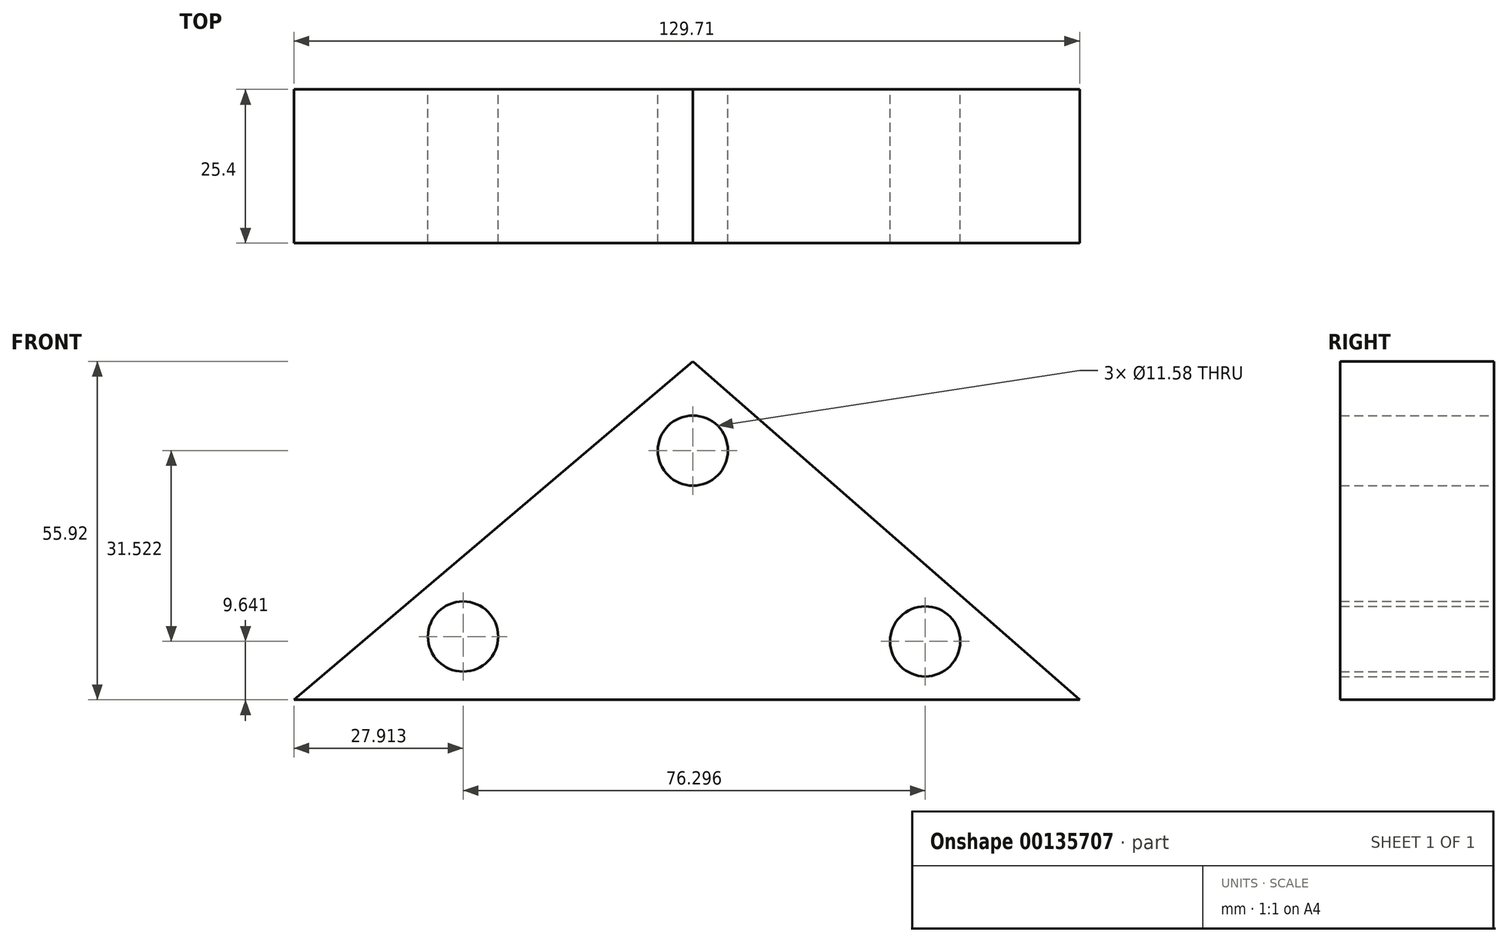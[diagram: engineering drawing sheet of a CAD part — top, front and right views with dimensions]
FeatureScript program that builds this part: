
annotation { "Feature Type Name" : "Feature", "Feature Type Description" : "" }
export const myFeature = defineFeature(function(context is Context, id is Id, definition is map)
    precondition{}
    {
        {
            var Q0;
            Q0=qCreatedBy(makeId("Front.planeOp"),FACE);
            var sketch = newSketch(context, id + "F0", { "sketchPlane" : qUnion([Q0])});
            skLineSegment(sketch, "E0", {"start": v(0, 0) * mm, "end": v(-65.86, -55.92) * mm});
            skLineSegment(sketch, "E1", {"start": v(0, 0) * mm, "end": v(63.85, -55.92) * mm});
            skLineSegment(sketch, "E2", {"start": v(-65.86, -55.92) * mm, "end": v(63.85, -55.92) * mm});
            skCircle(sketch, "E3", {"center": v(0, -14.76) * mm, "radius": 5.8 * mm});
            skCircle(sketch, "E4", {"center": v(-37.95, -45.48) * mm, "radius": 5.8 * mm});
            skCircle(sketch, "E5", {"center": v(38.35, -46.28) * mm, "radius": 5.8 * mm});
            skSolve(sketch);
        }
        {
            var Q0;
            Q0=makeQuery(id+"F0.imprint","IMPRINT",FACE,{"disambiguationData":[TD([[makeQuery(id+"F0.imprint","IMPRINT",EDGE,{"derivedFrom":sQuery(id+"F0.wireOp",EDGE,"E0")}),1.0]])]});
            extrude(context, id + "F1", {"entities" : qUnion([Q0]), "depth" : 25.4 * mm});
        }
    });
